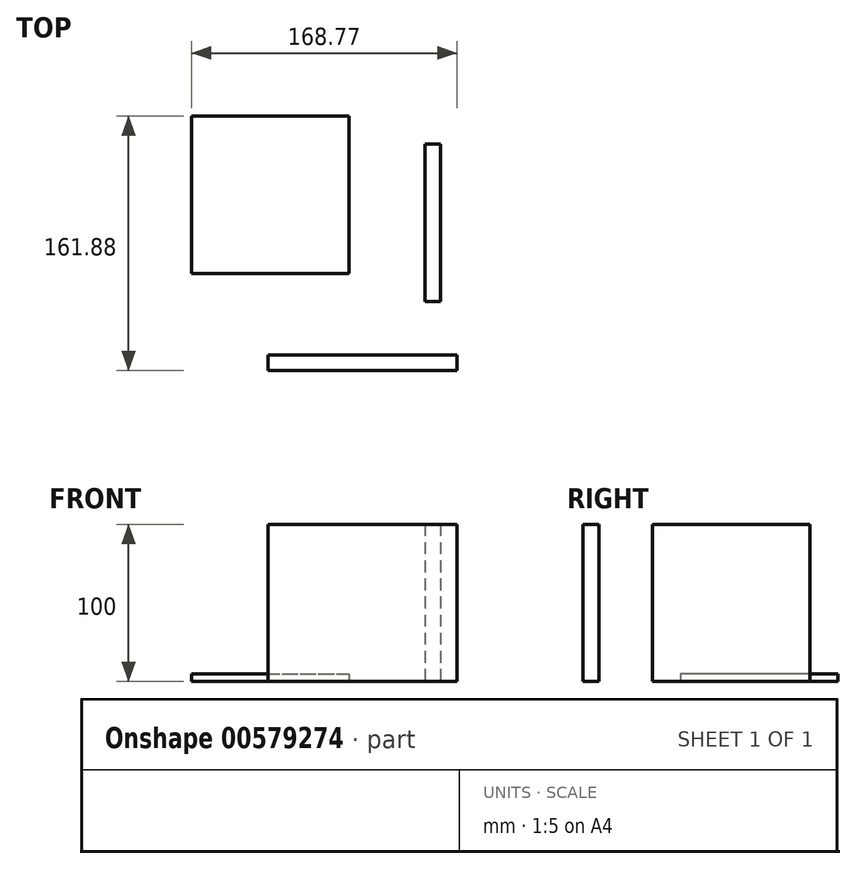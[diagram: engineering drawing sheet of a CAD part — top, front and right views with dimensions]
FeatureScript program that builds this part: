
annotation { "Feature Type Name" : "Feature", "Feature Type Description" : "" }
export const myFeature = defineFeature(function(context is Context, id is Id, definition is map)
    precondition{}
    {
        {
            var Q0;
            Q0=qCreatedBy(makeId("Top.planeOp"),FACE);
            var sketch = newSketch(context, id + "F0", { "sketchPlane" : qUnion([Q0])});
            skLineSegment(sketch, "E0.bottom", {"start": v(-106.27, 122.72) * mm, "end": v(-6.27, 122.72) * mm});
            skLineSegment(sketch, "E0.top", {"start": v(-106.27, 22.72) * mm, "end": v(-6.27, 22.72) * mm});
            skLineSegment(sketch, "E0.left", {"start": v(-106.27, 122.72) * mm, "end": v(-106.27, 22.72) * mm});
            skLineSegment(sketch, "E0.right", {"start": v(-6.27, 122.72) * mm, "end": v(-6.27, 22.72) * mm});
            skSolve(sketch);
        }
        {
            var Q0;
            Q0=makeQuery(id+"F0.imprint","IMPRINT",FACE,{"disambiguationData":[TD([[makeQuery(id+"F0.imprint","IMPRINT",EDGE,{"derivedFrom":sQuery(id+"F0.wireOp",EDGE,"E0.bottom")}),-1.0]])]});
            extrude(context, id + "F1", {"entities" : qUnion([Q0]), "depth" : 5 * mm, "offsetDistance" : 25 * mm});
        }
        {
            var Q0;
            Q0=qCreatedBy(makeId("Top.planeOp"),FACE);
            var sketch = newSketch(context, id + "F2", { "sketchPlane" : qUnion([Q0])});
            skLineSegment(sketch, "E1.bottom", {"start": v(41.95, 104.75) * mm, "end": v(51.95, 104.75) * mm});
            skLineSegment(sketch, "E1.top", {"start": v(41.95, 4.75) * mm, "end": v(51.95, 4.75) * mm});
            skLineSegment(sketch, "E1.left", {"start": v(41.95, 104.75) * mm, "end": v(41.95, 4.75) * mm});
            skLineSegment(sketch, "E1.right", {"start": v(51.95, 104.75) * mm, "end": v(51.95, 4.75) * mm});
            skSolve(sketch);
        }
        {
            var Q0;
            Q0=qCreatedBy(makeId("Top.planeOp"),FACE);
            var sketch = newSketch(context, id + "F3", { "sketchPlane" : qUnion([Q0])});
            skLineSegment(sketch, "E2.bottom", {"start": v(-57.5, -29.16) * mm, "end": v(62.5, -29.16) * mm});
            skLineSegment(sketch, "E2.top", {"start": v(-57.5, -39.16) * mm, "end": v(62.5, -39.16) * mm});
            skLineSegment(sketch, "E2.left", {"start": v(-57.5, -29.16) * mm, "end": v(-57.5, -39.16) * mm});
            skLineSegment(sketch, "E2.right", {"start": v(62.5, -29.16) * mm, "end": v(62.5, -39.16) * mm});
            skSolve(sketch);
        }
        {
            var Q0;
            Q0=makeQuery(id+"F3.imprint","IMPRINT",FACE,{"disambiguationData":[TD([[makeQuery(id+"F3.imprint","IMPRINT",EDGE,{"derivedFrom":sQuery(id+"F3.wireOp",EDGE,"E2.bottom")}),-1.0]])]});
            extrude(context, id + "F4", {"entities" : qUnion([Q0]), "depth" : 100 * mm, "offsetDistance" : 25 * mm});
        }
        {
            var Q0;
            Q0=makeQuery(id+"F2.imprint","IMPRINT",FACE,{"disambiguationData":[TD([[makeQuery(id+"F2.imprint","IMPRINT",EDGE,{"derivedFrom":sQuery(id+"F2.wireOp",EDGE,"E1.bottom")}),-1.0]])]});
            extrude(context, id + "F5", {"entities" : qUnion([Q0]), "depth" : 100 * mm, "offsetDistance" : 25 * mm});
        }
    });
